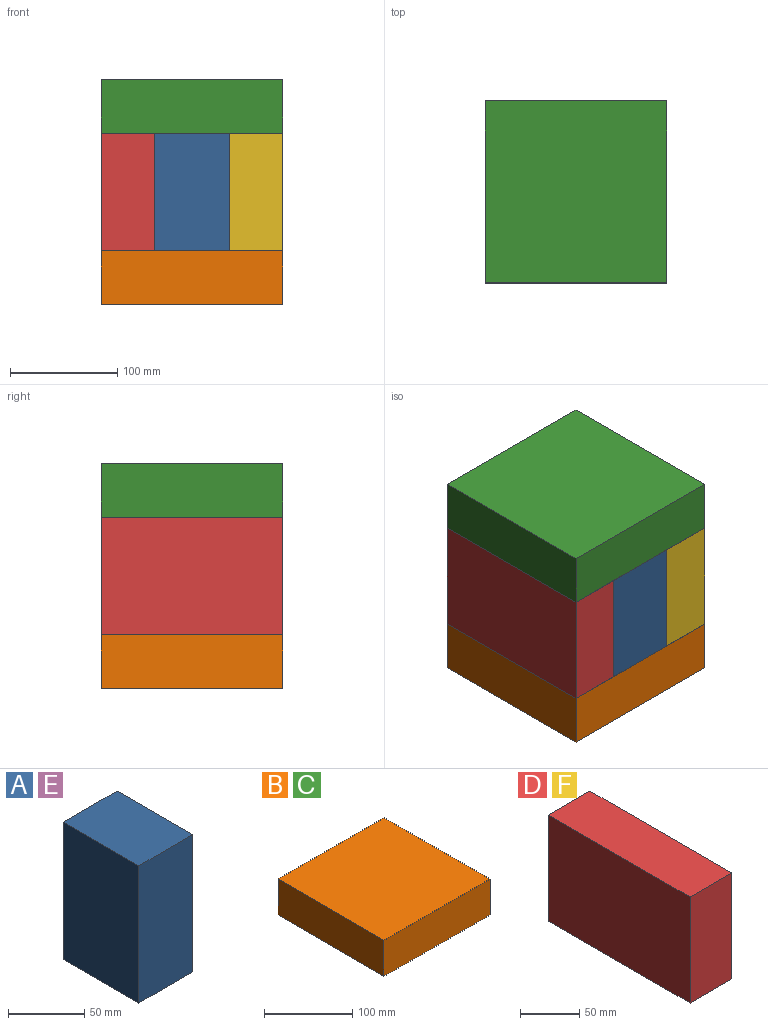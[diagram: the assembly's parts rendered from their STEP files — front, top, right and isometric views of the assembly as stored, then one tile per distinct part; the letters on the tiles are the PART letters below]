
ASSEMBLY  parts=6 mates=5
PART A: 6 faces, bbox 50x70x110 mm
  f0: plane 110x70mm, normal (-1,0,0), area 7700mm2, adj f1,f3,f4,f5
  f1: plane 110x50mm, normal (0,-1,0), area 5500mm2, adj f0,f2,f4,f5
  f2: plane 110x70mm, normal (1,0,0), area 7700mm2, adj f1,f3,f4,f5
  f3: plane 110x50mm, normal (0,1,0), area 5500mm2, adj f0,f2,f4,f5
  f4: plane 70x50mm, normal (0,0,1), area 3500mm2, adj f0,f1,f2,f3
  f5: plane 70x50mm, normal (0,0,-1), area 3500mm2, adj f0,f1,f2,f3
PART B: 6 faces, bbox 170x170x50 mm
  f0: plane 170x50mm, normal (-1,0,0), area 8500mm2, adj f1,f3,f4,f5
  f1: plane 170x50mm, normal (0,-1,0), area 8500mm2, adj f0,f2,f4,f5
  f2: plane 170x50mm, normal (1,0,0), area 8500mm2, adj f1,f3,f4,f5
  f3: plane 170x50mm, normal (0,1,0), area 8500mm2, adj f0,f2,f4,f5
  f4: plane 170x170mm, normal (0,0,1), area 28900mm2, adj f0,f1,f2,f3
  f5: plane 170x170mm, normal (0,0,-1), area 28900mm2, adj f0,f1,f2,f3
PART C: same geometry as B
PART D: 6 faces, bbox 50x170x110 mm
  f0: plane 170x110mm, normal (-1,0,0), area 18700mm2, adj f1,f3,f4,f5
  f1: plane 110x50mm, normal (0,-1,0), area 5500mm2, adj f0,f2,f4,f5
  f2: plane 170x110mm, normal (1,0,0), area 18700mm2, adj f1,f3,f4,f5
  f3: plane 110x50mm, normal (0,1,0), area 5500mm2, adj f0,f2,f4,f5
  f4: plane 170x50mm, normal (0,0,1), area 8500mm2, adj f0,f1,f2,f3
  f5: plane 170x50mm, normal (0,0,-1), area 8500mm2, adj f0,f1,f2,f3
PART E: same geometry as A
PART F: same geometry as D
PLACE A rot(axis=(0,0,1),90deg) t=(2.95,-72.71,10.76)mm
PLACE B t=(2.95,-12.71,-39.24)mm
PLACE C t=(2.95,-12.71,120.76)mm
PLACE D t=(-57.05,-12.71,10.76)mm
PLACE E rot(axis=(0,0,1),90deg) t=(2.95,47.29,10.76)mm
PLACE F t=(62.95,-12.71,10.76)mm
MATE fastened E.f5 <-> B.f4  axis (0,0,-1) through (2.95,72.29,10.76)mm
MATE fastened C.f5 <-> F.f4  axis (0,0,-1) through (87.95,-12.71,120.76)mm
MATE fastened D.f5 <-> B.f4  axis (0,0,-1) through (-82.05,-12.71,10.76)mm
MATE fastened F.f5 <-> B.f4  axis (0,0,-1) through (87.95,-12.71,10.76)mm
MATE fastened A.f5 <-> B.f4  axis (0,0,-1) through (2.95,-97.71,10.76)mm
